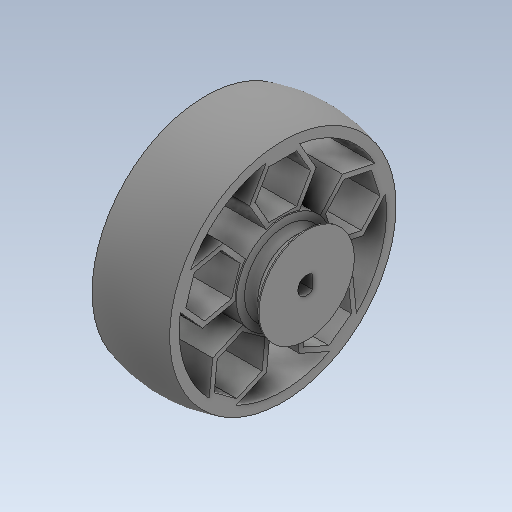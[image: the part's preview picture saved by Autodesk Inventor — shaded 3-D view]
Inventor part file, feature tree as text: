
AUTODESK INVENTOR PART (.ipt)
format: ipt  version: 2020 (Build 240168000, 168)  size: 414,720 bytes
history: native  units: in
note: dims shown in document units (in); Inventor stores cm internally (conversion verified against a paired STEP export)
features: sketch x4, extrude x2, revolve x2, projected_geometry x1
ambient origin geometry x8: Origin, YZ Plane, XZ Plane, XY Plane, X Axis, Y Axis, Z Axis, Center Point
bodies: Solid1 (feature_tree)
feature tree (9):
  extrude  "Extrusion1"  Depth=0.0394in
  sketch  "Sketch3"  dims[d6=0.6299in d7=0.1575in]
  revolve  "Revolution1"  [1 undecoded]
  extrude  "Extrusion2"  Depth=0.1575in
  revolve  "Revolution2"  [1 undecoded]
  sketch  "Sketch1"  dims[d0=0.1181in d1=0.0394in]
  sketch  "Sketch2"  dims[d3=1.4961in d4=0.1181in]
  projected_geometry  "Projected Loop1"
  sketch  "Sketch4"  dims[d8=0.0in d9=1.4961in d10=0.063in d11=0.0315in d16=0.5118in d17=0.0in d19=360.0deg d20=0.0787in d24=0.0394in d25=90.0deg d26=45.0deg d28=0.0079in d29=1.9685in d31=360.0deg]
note: 2 required parameter values undecoded (feature->parameter linkage not recoverable at this tier; creation-order binding heuristic only, values carry confidence <= 0.55)
